# Revit family: E_FF109 Downlighter Cover(150,200,250mm)
name_source: partatom
category: Specialty Equipment
revit_build: Autodesk Revit 2015 (Build: 20160512_0715(x64)
units: mm (PartAtom-declared; Revit-internal decimal feet)

## types (3) — shared parameters
IFC Classification = Building Element Proxy
Length = 150 mm
Manufacturer = Tenmat ltd
Material/Grade = Firefly 109
Performance = BS EN 1366-3:2009 & BS 476, ETA-12/0332, 1224-CPR-0341, CE Marked
URL = https://www.tenmat.com
Width = 150 mm
Youtube Clip = https://www.youtube.com

## per-type parameters (varying)
| type | Cut-Out Size | Description | Height | Radius | Tenmat Item Number | Wall Thickness |
| 150x150mm | 50-75mm | Firefly 109 150x150mm Downlighter Cover | 160 mm | 75 mm | I109MC01000150015004
I109MC01000150015004
I109MC01000150015004
I109MC01000150015004 | 8 mm  [stored 0.0262467 ft] |
| 200x200mm | 75-100mm | Firefly 109 200x200mm Downlighter Cover | 210 mm | 100 mm  [stored 0.328084 ft] | I109MC01000200020003 | 8 mm  [stored 0.0262467 ft] |
| 250x250mm | 100-140mm | Firefly 109 250x250mm Downlighter Cover | 260 mm  [stored 0.853018 ft] | 130 mm  [stored 0.426509 ft] | I109MC01000250025002 | 9 mm  [stored 0.0295276 ft] |

note: [stored X ft] marks values corroborated as IEEE doubles in the binary element streams (Revit-internal decimal feet)

## geometry (parser evidence)
native form markers: Blend x2, Sweep x3
no freeform markers — native parametric forms only
